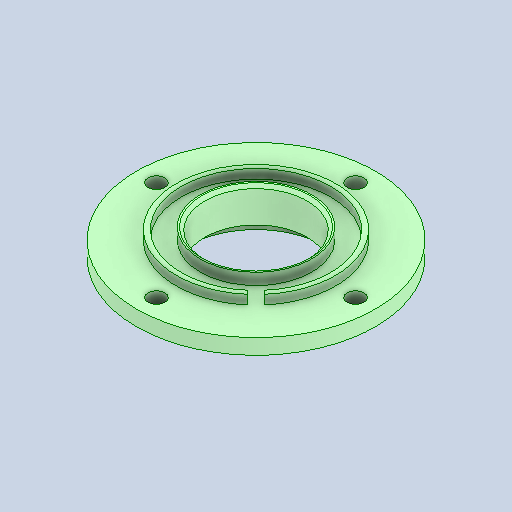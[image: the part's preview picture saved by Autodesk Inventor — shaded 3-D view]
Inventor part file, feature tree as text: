
AUTODESK INVENTOR PART (.ipt)
format: ipt  version: 2024.1 (Build 281209000, 209)  size: 179,712 bytes
history: native  units: in
note: dims shown in document units (in); Inventor stores cm internally (conversion verified against a paired STEP export)
features: chamfer x1
ambient origin geometry x8: Origin, YZ Plane, XZ Plane, XY Plane, X Axis, Y Axis, Z Axis, Center Point
bodies: Solid1 (feature_tree)
feature tree (1):
  chamfer  "Chamfer1"  [1 undecoded]
note: 1 required parameter value undecoded (feature->parameter linkage not recoverable at this tier; creation-order binding heuristic only, values carry confidence <= 0.55)
